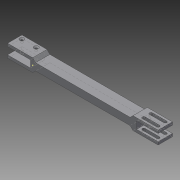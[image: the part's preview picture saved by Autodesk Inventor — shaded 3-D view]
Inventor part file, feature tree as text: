
AUTODESK INVENTOR PART (.ipt)
format: ipt  version: 2015 (Build 190159000, 159)  size: 198,144 bytes
history: native  units: mm
features: sketch x9, extrude x7, chamfer x2, hole x1
ambient origin geometry x8: Origin, YZ Plane, XZ Plane, XY Plane, X Axis, Y Axis, Z Axis, Center Point
bodies: Solid1 (feature_tree)
feature tree (19):
  extrude  "Extrusion1"  Depth=20.0mm
  sketch  "Sketch2"  dims[d2=10.0mm d3=0.0mm d4=4.0mm]
  extrude  "Extrusion2"  Depth=4.0mm
  extrude  "Extrusion3"  Depth=4.0mm TaperAngle=0.0deg
  hole  "Hole1"  [1 undecoded]
  chamfer  "Chamfer1"  Distance=4.0mm Angle=45.0deg
  extrude  "Extrusion4"  Depth=4.0mm
  extrude  "Extrusion5"  Depth=20.0mm
  chamfer  "Chamfer2"  Distance=20.0mm
  extrude  "Extrusion6"  Depth=30.0mm
  extrude  "Extrusion7"  Depth=30.0mm
  sketch  "Sketch1"  dims[d0=150.0mm d1=20.0mm]
  sketch  "Sketch3"  dims[d5=4.0mm d6=5.0mm d7=0.0mm]
  sketch  "Sketch4"  dims[d8=30.0mm d9=0.0mm d10=5.0mm]
  sketch  "Sketch5"  dims[d11=5.0mm]
  sketch  "Sketch6"  dims[d12=5.0mm]
  sketch  "Sketch7"  dims[d13=5.0mm]
  sketch  "Sketch8"  dims[d14=3.0mm d15=6.0mm d16=6.0mm d17=2.0mm d18=90.0deg d19=30.0mm d20=20.594885mm d21=4.0mm d22=2.0mm d23=45.0deg]
  sketch  "Sketch9"  dims[d24=4.0mm d25=4.0mm d26=5.0mm d27=20.0mm d28=0.0mm d29=30.0mm d30=30.0mm d31=4.0mm d32=4.0mm d33=20.0mm d34=0.0mm d35=4.0mm d36=2.0mm d37=45.0deg d38=5.0mm d39=5.0mm d40=5.0mm d41=5.0mm d42=5.0mm d43=5.0mm d44=5.0mm d45=5.0mm d46=4.0mm d47=4.0mm d48=4.0mm d49=4.0mm d50=20.0mm d51=0.0mm d52=1.851607mm d53=20.0mm d54=0.0mm]
note: 1 required parameter value undecoded (feature->parameter linkage not recoverable at this tier; creation-order binding heuristic only, values carry confidence <= 0.55)
